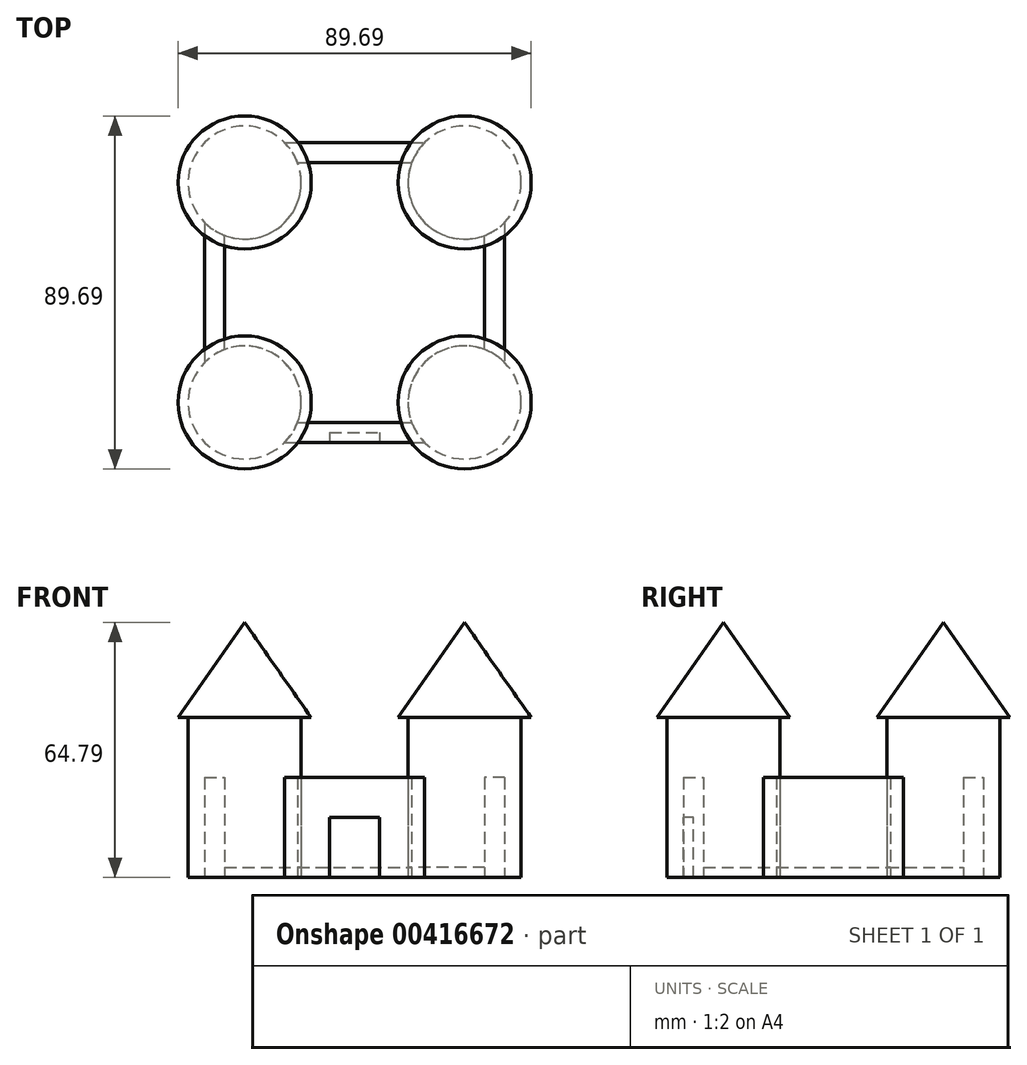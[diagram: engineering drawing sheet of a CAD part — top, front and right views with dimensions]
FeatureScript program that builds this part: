
annotation { "Feature Type Name" : "Feature", "Feature Type Description" : "" }
export const myFeature = defineFeature(function(context is Context, id is Id, definition is map)
    precondition{}
    {
        {
            var Q0;
            Q0=qCreatedBy(makeId("Top.planeOp"),FACE);
            var sketch = newSketch(context, id + "F0", { "sketchPlane" : qUnion([Q0])});
            skLineSegment(sketch, "E0.bottom", {"start": v(-37.26, 36.88) * mm, "end": v(38.94, 36.88) * mm});
            skLineSegment(sketch, "E0.top", {"start": v(-37.26, -39.32) * mm, "end": v(38.94, -39.32) * mm});
            skLineSegment(sketch, "E0.left", {"start": v(-37.26, 36.88) * mm, "end": v(-37.26, -39.32) * mm});
            skLineSegment(sketch, "E0.right", {"start": v(38.94, 36.88) * mm, "end": v(38.94, -39.32) * mm});
            skCircle(sketch, "E1", {"center": v(-27.1, 26.72) * mm, "radius": 14.37 * mm});
            skPoint(sketch, "E1.second.point", {"position": v(-37.26, 16.56) * mm});
            skPoint(sketch, "E1.third.point", {"position": v(-16.94, 36.88) * mm});
            skCircle(sketch, "E2", {"center": v(-27.1, -29.16) * mm, "radius": 14.37 * mm});
            skPoint(sketch, "E2.second.point", {"position": v(-37.26, -19) * mm});
            skPoint(sketch, "E2.third.point", {"position": v(-16.94, -39.32) * mm});
            skCircle(sketch, "E3", {"center": v(28.78, 26.72) * mm, "radius": 14.37 * mm});
            skPoint(sketch, "E3.second.point", {"position": v(18.62, 36.88) * mm});
            skPoint(sketch, "E3.third.point", {"position": v(38.94, 16.56) * mm});
            skCircle(sketch, "E4", {"center": v(28.78, -29.16) * mm, "radius": 14.37 * mm});
            skPoint(sketch, "E4.second.point", {"position": v(38.94, -19) * mm});
            skPoint(sketch, "E4.third.point", {"position": v(18.62, -39.32) * mm});
            skLineSegment(sketch, "E5", {"start": v(-32.18, -15.72) * mm, "end": v(-32.18, 13.28) * mm});
            skLineSegment(sketch, "E6", {"start": v(-13.66, 31.8) * mm, "end": v(15.34, 31.8) * mm});
            skLineSegment(sketch, "E7", {"start": v(-13.66, -34.24) * mm, "end": v(15.34, -34.24) * mm});
            skLineSegment(sketch, "E8", {"start": v(33.86, -15.72) * mm, "end": v(33.86, 13.28) * mm});
            skSolve(sketch);
        }
        {
            var Q0;
            {var subQ5=sQuery(id+"F0.wireOp",EDGE,"E5");Q0=makeQuery(id+"F0.imprint","IMPRINT",FACE,{"disambiguationData":[TD([[makeQuery(id+"F0.imprint","IMPRINT",EDGE,{"derivedFrom":subQ5}),-1.0]])]});}
            extrude(context, id + "F1", {"entities" : qUnion([Q0]), "depth" : 2.54 * mm});
        }
        {
            var Q0;
            {var subQ5=sQuery(id+"F0.wireOp",EDGE,"E8");Q0=makeQuery(id+"F0.imprint","IMPRINT",FACE,{"disambiguationData":[TD([[makeQuery(id+"F0.imprint","IMPRINT",EDGE,{"derivedFrom":subQ5}),-1.0]])]});}
            var Q1;
            {var subQ5=sQuery(id+"F0.wireOp",EDGE,"E7");Q1=makeQuery(id+"F0.imprint","IMPRINT",FACE,{"disambiguationData":[TD([[makeQuery(id+"F0.imprint","IMPRINT",EDGE,{"derivedFrom":subQ5}),-1.0]])]});}
            var Q2;
            {var subQ5=sQuery(id+"F0.wireOp",EDGE,"E5");Q2=makeQuery(id+"F0.imprint","IMPRINT",FACE,{"disambiguationData":[TD([[makeQuery(id+"F0.imprint","IMPRINT",EDGE,{"derivedFrom":subQ5}),1.0]])]});}
            var Q3;
            {var subQ5=sQuery(id+"F0.wireOp",EDGE,"E6");Q3=makeQuery(id+"F0.imprint","IMPRINT",FACE,{"disambiguationData":[TD([[makeQuery(id+"F0.imprint","IMPRINT",EDGE,{"derivedFrom":subQ5}),1.0]])]});}
            extrude(context, id + "F2", {"entities" : qUnion([Q0, Q1, Q2, Q3]), "depth" : 25.4 * mm});
        }
        {
            var Q0;
            {var subQ0=sQuery(id+"F0.wireOp",EDGE,"E3");var subQ1=sQuery(id+"F0.wireOp",EDGE,"E0.right");var subQ3=makeQuery(id+"F0.imprint","INTERSECT",VERTEX,{"derivedFrom":[subQ1,subQ0]});Q0=makeQuery(id+"F0.imprint","IMPRINT",FACE,{"disambiguationData":[TD([[makeQuery(id+"F0.imprint","IMPRINT",EDGE,{"disambiguationData":[TD([[subQ3,1.0]])],"derivedFrom":subQ1}),1.0]])]});}
            var Q1;
            {var subQ0=sQuery(id+"F0.wireOp",EDGE,"E3");var subQ1=makeQuery(id+"F0.imprint","INTERSECT",VERTEX,{"derivedFrom":[subQ0,sQuery(id+"F0.wireOp",EDGE,"E6")]});Q1=makeQuery(id+"F0.imprint","IMPRINT",FACE,{"disambiguationData":[TD([[makeQuery(id+"F0.imprint","IMPRINT",EDGE,{"disambiguationData":[TD([[subQ1,1.0]])],"derivedFrom":subQ0}),1.0]])]});}
            var Q2;
            {var subQ0=sQuery(id+"F0.wireOp",EDGE,"E3");var subQ1=sQuery(id+"F0.wireOp",EDGE,"E0.bottom");var subQ3=makeQuery(id+"F0.imprint","INTERSECT",VERTEX,{"derivedFrom":[subQ1,subQ0]});Q2=makeQuery(id+"F0.imprint","IMPRINT",FACE,{"disambiguationData":[TD([[makeQuery(id+"F0.imprint","IMPRINT",EDGE,{"disambiguationData":[TD([[subQ3,-1.0]])],"derivedFrom":subQ1}),1.0]])]});}
            var Q3;
            {var subQ0=sQuery(id+"F0.wireOp",EDGE,"E4");var subQ1=sQuery(id+"F0.wireOp",EDGE,"E0.right");var subQ3=makeQuery(id+"F0.imprint","INTERSECT",VERTEX,{"derivedFrom":[subQ1,subQ0]});Q3=makeQuery(id+"F0.imprint","IMPRINT",FACE,{"disambiguationData":[TD([[makeQuery(id+"F0.imprint","IMPRINT",EDGE,{"disambiguationData":[TD([[subQ3,-1.0]])],"derivedFrom":subQ1}),1.0]])]});}
            var Q4;
            {var subQ0=sQuery(id+"F0.wireOp",EDGE,"E4");var subQ1=sQuery(id+"F0.wireOp",EDGE,"E0.top");var subQ3=makeQuery(id+"F0.imprint","INTERSECT",VERTEX,{"derivedFrom":[subQ1,subQ0]});Q4=makeQuery(id+"F0.imprint","IMPRINT",FACE,{"disambiguationData":[TD([[makeQuery(id+"F0.imprint","IMPRINT",EDGE,{"disambiguationData":[TD([[subQ3,-1.0]])],"derivedFrom":subQ1}),-1.0]])]});}
            var Q5;
            {var subQ0=sQuery(id+"F0.wireOp",EDGE,"E4");var subQ2=makeQuery(id+"F0.imprint","INTERSECT",VERTEX,{"derivedFrom":[subQ0,sQuery(id+"F0.wireOp",EDGE,"E8")]});Q5=makeQuery(id+"F0.imprint","IMPRINT",FACE,{"disambiguationData":[TD([[makeQuery(id+"F0.imprint","IMPRINT",EDGE,{"disambiguationData":[TD([[subQ2,1.0]])],"derivedFrom":subQ0}),1.0]])]});}
            var Q6;
            {var subQ0=sQuery(id+"F0.wireOp",EDGE,"E2");var subQ1=sQuery(id+"F0.wireOp",EDGE,"E0.top");var subQ3=makeQuery(id+"F0.imprint","INTERSECT",VERTEX,{"derivedFrom":[subQ1,subQ0]});Q6=makeQuery(id+"F0.imprint","IMPRINT",FACE,{"disambiguationData":[TD([[makeQuery(id+"F0.imprint","IMPRINT",EDGE,{"disambiguationData":[TD([[subQ3,1.0]])],"derivedFrom":subQ1}),-1.0]])]});}
            var Q7;
            {var subQ0=sQuery(id+"F0.wireOp",EDGE,"E2");var subQ4=makeQuery(id+"F0.imprint","INTERSECT",VERTEX,{"derivedFrom":[subQ0,sQuery(id+"F0.wireOp",EDGE,"E5")]});Q7=makeQuery(id+"F0.imprint","IMPRINT",FACE,{"disambiguationData":[TD([[makeQuery(id+"F0.imprint","IMPRINT",EDGE,{"disambiguationData":[TD([[subQ4,-1.0]])],"derivedFrom":subQ0}),1.0]])]});}
            var Q8;
            {var subQ0=sQuery(id+"F0.wireOp",EDGE,"E2");var subQ1=sQuery(id+"F0.wireOp",EDGE,"E0.left");var subQ3=makeQuery(id+"F0.imprint","INTERSECT",VERTEX,{"derivedFrom":[subQ1,subQ0]});Q8=makeQuery(id+"F0.imprint","IMPRINT",FACE,{"disambiguationData":[TD([[makeQuery(id+"F0.imprint","IMPRINT",EDGE,{"disambiguationData":[TD([[subQ3,-1.0]])],"derivedFrom":subQ1}),-1.0]])]});}
            var Q9;
            {var subQ0=sQuery(id+"F0.wireOp",EDGE,"E1");var subQ1=sQuery(id+"F0.wireOp",EDGE,"E0.left");var subQ3=makeQuery(id+"F0.imprint","INTERSECT",VERTEX,{"derivedFrom":[subQ1,subQ0]});Q9=makeQuery(id+"F0.imprint","IMPRINT",FACE,{"disambiguationData":[TD([[makeQuery(id+"F0.imprint","IMPRINT",EDGE,{"disambiguationData":[TD([[subQ3,1.0]])],"derivedFrom":subQ1}),-1.0]])]});}
            var Q10;
            {var subQ0=sQuery(id+"F0.wireOp",EDGE,"E1");var subQ1=makeQuery(id+"F0.imprint","INTERSECT",VERTEX,{"derivedFrom":[subQ0,sQuery(id+"F0.wireOp",EDGE,"E6")]});Q10=makeQuery(id+"F0.imprint","IMPRINT",FACE,{"disambiguationData":[TD([[makeQuery(id+"F0.imprint","IMPRINT",EDGE,{"disambiguationData":[TD([[subQ1,-1.0]])],"derivedFrom":subQ0}),1.0]])]});}
            var Q11;
            {var subQ0=sQuery(id+"F0.wireOp",EDGE,"E1");var subQ1=sQuery(id+"F0.wireOp",EDGE,"E0.bottom");var subQ3=makeQuery(id+"F0.imprint","INTERSECT",VERTEX,{"derivedFrom":[subQ1,subQ0]});Q11=makeQuery(id+"F0.imprint","IMPRINT",FACE,{"disambiguationData":[TD([[makeQuery(id+"F0.imprint","IMPRINT",EDGE,{"disambiguationData":[TD([[subQ3,1.0]])],"derivedFrom":subQ1}),1.0]])]});}
            extrude(context, id + "F3", {"entities" : qUnion([Q0, Q1, Q2, Q3, Q4, Q5, Q6, Q7, Q8, Q9, Q10, Q11]), "depth" : 40.64 * mm});
        }
        {
            var Q0;
            Q0=makeQuery(id+"F3.opExtrude","CAP_FACE",FACE,{"disambiguationData":[OSD([sQuery(id+"F0.wireOp",EDGE,"E2")])],"isStart":false});
            var sketch = newSketch(context, id + "F4", { "sketchPlane" : qUnion([Q0])});
            skCircle(sketch, "E9", {"center": v(-27.1, -29.16) * mm, "radius": 16.9 * mm});
            skSolve(sketch);
        }
        {
            var Q0;
            Q0 = qSketchRegion(id + "F4", true);
            extrude(context, id + "F5", {"entities" : qUnion([Q0]), "operationType" : NewBodyOperationType.ADD, "depth" : 25.4 * mm, "hasDraft" : true, "draftAngle" : 35 * degree, "draftPullDirection" : true});
        }
        {
            var Q0;
            Q0=makeQuery(id+"F3.opExtrude","CAP_FACE",FACE,{"disambiguationData":[OSD([sQuery(id+"F0.wireOp",EDGE,"E1")])],"isStart":false});
            var sketch = newSketch(context, id + "F6", { "sketchPlane" : qUnion([Q0])});
            skCircle(sketch, "E10", {"center": v(-27.1, 26.72) * mm, "radius": 16.9 * mm});
            skSolve(sketch);
        }
        {
            var Q0;
            Q0 = qSketchRegion(id + "F6", true);
            extrude(context, id + "F7", {"entities" : qUnion([Q0]), "operationType" : NewBodyOperationType.ADD, "depth" : 25.4 * mm, "hasDraft" : true, "draftAngle" : 35 * degree, "draftPullDirection" : true});
        }
        {
            var Q0;
            Q0=makeQuery(id+"F3.opExtrude","CAP_FACE",FACE,{"disambiguationData":[OSD([sQuery(id+"F0.wireOp",EDGE,"E3")])],"isStart":false});
            var sketch = newSketch(context, id + "F8", { "sketchPlane" : qUnion([Q0])});
            skCircle(sketch, "E11", {"center": v(28.78, 26.72) * mm, "radius": 16.9 * mm});
            skSolve(sketch);
        }
        {
            var Q0;
            Q0 = qSketchRegion(id + "F8", true);
            extrude(context, id + "F9", {"entities" : qUnion([Q0]), "operationType" : NewBodyOperationType.ADD, "depth" : 25.4 * mm, "hasDraft" : true, "draftAngle" : 35 * degree, "draftPullDirection" : true});
        }
        {
            var Q0;
            Q0=makeQuery(id+"F3.opExtrude","CAP_FACE",FACE,{"disambiguationData":[OSD([sQuery(id+"F0.wireOp",EDGE,"E4")])],"isStart":false});
            var sketch = newSketch(context, id + "F10", { "sketchPlane" : qUnion([Q0])});
            skCircle(sketch, "E12", {"center": v(28.78, -29.16) * mm, "radius": 16.9 * mm});
            skSolve(sketch);
        }
        {
            var Q0;
            Q0 = qSketchRegion(id + "F10", true);
            extrude(context, id + "F11", {"entities" : qUnion([Q0]), "operationType" : NewBodyOperationType.ADD, "depth" : 25.4 * mm, "hasDraft" : true, "draftAngle" : 35 * degree, "draftPullDirection" : true});
        }
        {
            var Q0;
            Q0=makeQuery(id+"F2.opExtrude","SWEPT_FACE",FACE,{"disambiguationData":[OSD([sQuery(id+"F0.wireOp",EDGE,"E0.top")])]});
            var sketch = newSketch(context, id + "F12", { "sketchPlane" : qUnion([Q0])});
            skLineSegment(sketch, "E13.bottom", {"start": v(-5.51, 0) * mm, "end": v(7.19, 0) * mm});
            skLineSegment(sketch, "E13.top", {"start": v(-5.51, 15.24) * mm, "end": v(7.19, 15.24) * mm});
            skLineSegment(sketch, "E13.left", {"start": v(-5.51, 0) * mm, "end": v(-5.51, 15.24) * mm});
            skLineSegment(sketch, "E13.right", {"start": v(7.19, 0) * mm, "end": v(7.19, 15.24) * mm});
            skSolve(sketch);
        }
        {
            var Q0;
            Q0=makeQuery(id+"F12.imprint","IMPRINT",FACE,{"disambiguationData":[TD([[makeQuery(id+"F12.imprint","IMPRINT",EDGE,{"derivedFrom":sQuery(id+"F12.wireOp",EDGE,"E13.bottom")}),1.0]])]});
            extrude(context, id + "F13", {"entities" : qUnion([Q0]), "operationType" : NewBodyOperationType.REMOVE, "oppositeDirection" : true, "depth" : 2.54 * mm});
        }
    });
